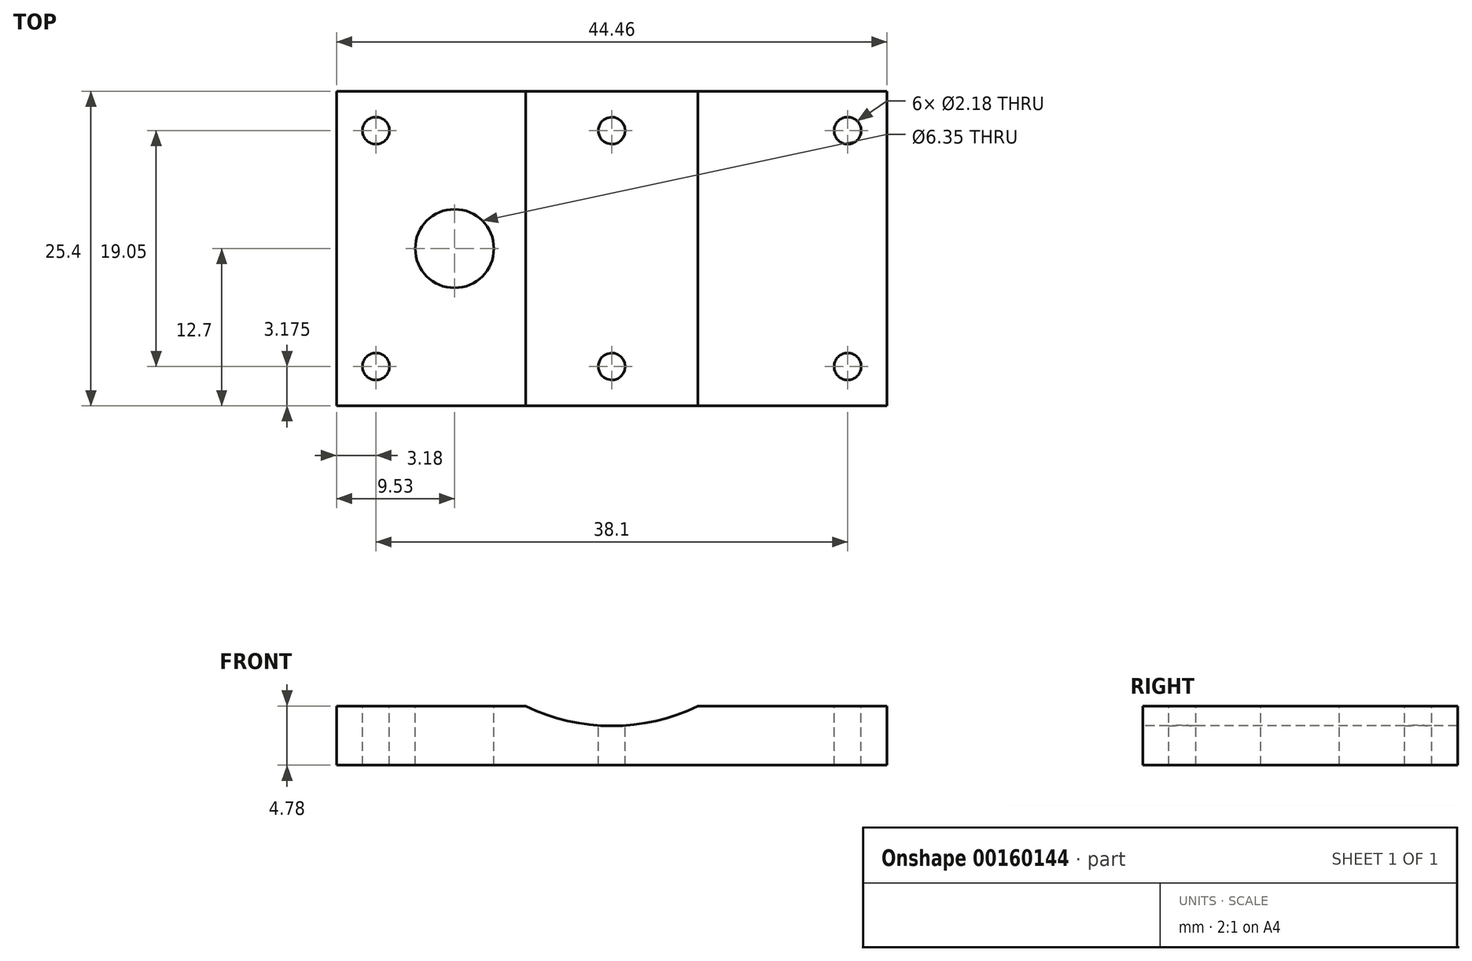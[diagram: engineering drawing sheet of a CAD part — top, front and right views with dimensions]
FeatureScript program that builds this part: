
annotation { "Feature Type Name" : "Feature", "Feature Type Description" : "" }
export const myFeature = defineFeature(function(context is Context, id is Id, definition is map)
    precondition{}
    {
        {
            var Q0;
            Q0=qCreatedBy(makeId("Top.planeOp"),FACE);
            var sketch = newSketch(context, id + "F0", { "sketchPlane" : qUnion([Q0])});
            skLineSegment(sketch, "E0.bottom", {"start": v(22.23, -12.7) * mm, "end": v(-22.23, -12.7) * mm});
            skLineSegment(sketch, "E0.top", {"start": v(22.23, 12.7) * mm, "end": v(-22.23, 12.7) * mm});
            skLineSegment(sketch, "E0.left", {"start": v(22.23, -12.7) * mm, "end": v(22.23, 12.7) * mm});
            skLineSegment(sketch, "E0.right", {"start": v(-22.23, -12.7) * mm, "end": v(-22.23, 12.7) * mm});
            skPoint(sketch, "E0.middle", {"position": v(0, 0) * mm});
            skSolve(sketch);
        }
        {
            var Q0;
            Q0 = qSketchRegion(id + "F0", true);
            extrude(context, id + "F1", {"entities" : qUnion([Q0]), "depth" : 4.78 * mm});
        }
        {
            var Q0;
            Q0=makeQuery(id+"F1.opExtrude","CAP_FACE",FACE,{"disambiguationData":[OSD([sQuery(id+"F0.wireOp",EDGE,"E0.bottom"),sQuery(id+"F0.wireOp",EDGE,"E0.top"),sQuery(id+"F0.wireOp",EDGE,"E0.left"),sQuery(id+"F0.wireOp",EDGE,"E0.right")])],"isStart":false});
            var sketch = newSketch(context, id + "F2", { "sketchPlane" : qUnion([Q0])});
            skLineSegment(sketch, "E1", {"start": v(-35.06, 9.53) * mm, "end": v(36.73, 9.53) * mm, "construction": true});
            skLineSegment(sketch, "E2", {"start": v(-34.7, -9.52) * mm, "end": v(45.44, -9.52) * mm, "construction": true});
            skLineSegment(sketch, "E3", {"start": v(19.05, 15.74) * mm, "end": v(19.05, -15.81) * mm, "construction": true});
            skLineSegment(sketch, "E4", {"start": v(-19.05, 15.46) * mm, "end": v(-19.05, -17.23) * mm, "construction": true});
            skCircle(sketch, "E5", {"center": v(-19.05, 9.53) * mm, "radius": 1.1 * mm});
            skCircle(sketch, "E6", {"center": v(19.05, 9.53) * mm, "radius": 1.1 * mm});
            skCircle(sketch, "E7", {"center": v(19.05, -9.52) * mm, "radius": 1.1 * mm});
            skCircle(sketch, "E8", {"center": v(-19.05, -9.52) * mm, "radius": 1.1 * mm});
            skLineSegment(sketch, "E9", {"start": v(-30.82, 0) * mm, "end": v(28.12, 0) * mm, "construction": true});
            skLineSegment(sketch, "E10", {"start": v(-12.7, 16.98) * mm, "end": v(-12.7, -16.1) * mm, "construction": true});
            skCircle(sketch, "E11", {"center": v(-12.7, 0) * mm, "radius": 3.18 * mm});
            skLineSegment(sketch, "E12", {"start": v(0, 15.56) * mm, "end": v(0, -17.7) * mm, "construction": true});
            skPoint(sketch, "E12.endSnap0", {"position": v(0, -12.7) * mm});
            skCircle(sketch, "E13", {"center": v(0, 9.53) * mm, "radius": 1.1 * mm});
            skCircle(sketch, "E14", {"center": v(0, -9.52) * mm, "radius": 1.1 * mm});
            skSolve(sketch);
        }
        {
            var Q0;
            Q0 = qSketchRegion(id + "F2", true);
            extrude(context, id + "F3", {"entities" : qUnion([Q0]), "operationType" : NewBodyOperationType.REMOVE, "endBound" : BoundingType.THROUGH_ALL, "oppositeDirection" : true, "depth" : 25.4 * mm});
        }
        {
            var Q0;
            Q0=makeQuery(id+"F1.opExtrude","SWEPT_FACE",FACE,{"disambiguationData":[OSD([sQuery(id+"F0.wireOp",EDGE,"E0.bottom")])]});
            var sketch = newSketch(context, id + "F4", { "sketchPlane" : qUnion([Q0])});
            skLineSegment(sketch, "E15", {"start": v(0, 0) * mm, "end": v(0, 21.26) * mm, "construction": true});
            skLineSegment(sketch, "E16", {"start": v(-16.1, 19.05) * mm, "end": v(13.17, 19.05) * mm, "construction": true});
            skCircle(sketch, "E17", {"center": v(0, 19.05) * mm, "radius": 15.88 * mm});
            skSolve(sketch);
        }
        {
            var Q0;
            Q0 = qSketchRegion(id + "F4", true);
            extrude(context, id + "F5", {"entities" : qUnion([Q0]), "operationType" : NewBodyOperationType.REMOVE, "endBound" : BoundingType.THROUGH_ALL, "oppositeDirection" : true, "depth" : 25.4 * mm});
        }
    });
